# Revit family: Gira_213800
name_source: partatom
category: Elektroinstallationen
revit_build: Autodesk Revit 2017 (Build: 20160225_1515(x64)
units: mm (PartAtom-declared; Revit-internal decimal feet)

## family parameters
Basisbauteil = Fläche
Beim Laden mit Abzugskörper schneiden = Nein
Bemaßung runder Anschluss = Durchmesser verwenden
Beschriftungsausrichtung beibehalten = Nein
Gemeinsam genutzt = Nein
Raumberechnungspunkt = Nein
Teiletyp = Normal

## types (1)
- Spannungsversorgung 1280 mA Drossel KNX REG
    Andere Bussysteme = sonstige
    BIM = https://media.live.bim.site 00_REG 6.rfa
    BIMSITE_PRODUCT_ID = d2853a5bf78b8d7a9cae491f6953783b0369dc1b
    Beschreibung = KNX Spannungsversorgung 1280 mA mit integrierter Drossel   Spannungsversorgungen zur Versorgung von KNX Geräten mit Busspannung.  Merkmale:  Ausgang mit integrierter Drossel zur Versorgung von KNX Buslinien.  Ausgang DC 30 V zur Versorgung zusätzlicher Geräte.  Nennstrom beliebig auf die Ausgänge aufteilbar.  Reset-Taster.  Kurzschlussfest.  Überspannungsfest.  Leerlaufsicher.  Geeignet für Betrieb in Anlagen mit Notstromversorgung.  Potenzialfreier Meldekontakt für Betriebs- und Diagnosemeldung.  Hinweise :  Montage auf DIN-Hutschiene.  VDE-Zulassung gemäß EN 60669-1, EN 60669-2-1.
    Breite in Teilungseinheiten = 4
    Busspannung pufferbar = Nein
    Bussystem Funkbus = Nein
    Bussystem KNX = Ja
    Bussystem KNX-Funk = Nein
    Bussystem LON = Nein
    Bussystem Powernet = Nein
    Datenblatt = https://media.live.bim.site
    Datenblatt 1 = https://media.live.bim.site
    GTIN = 4010337023241
    HAN = 213800
    HeinzeBIM = https://www.heinze.de
    Hersteller = Gira
    Ist System = Nein
    Ist Zubehör = Nein
    Kosten = 0 $
    Max. Ausgangsstrom = 1 A
    Mit LED-Anzeige = Nein
    Montageart = REG
    Produktseite = https://media.live.bim.site
    Typname = Spannungsversorgung 1280 mA Drossel KNX REG
    URL = https://www.gira.de
    Vorgabe-Ansicht = 1219 mm

## geometry (parser evidence)
native form markers: Sweep x2
no freeform markers — native parametric forms only
